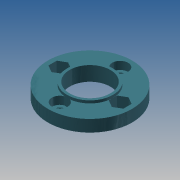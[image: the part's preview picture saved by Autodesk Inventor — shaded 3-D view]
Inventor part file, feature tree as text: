
AUTODESK INVENTOR PART (.ipt)
format: ipt  version: 2013 (Build 170138000, 138)  size: 146,944 bytes
history: native  units: mm
features: extrude x6, sketch x6, pattern_circular x2
ambient origin geometry x8: Origin, YZ Plane, XZ Plane, XY Plane, X Axis, Y Axis, Z Axis, Center Point
bodies: Solid1 (feature_tree)
feature tree (14):
  extrude  "Extrusion1"  Depth=4.5mm TaperAngle=0.0deg
  extrude  "Extrusion2"  Depth=1.0mm TaperAngle=0.0deg
  extrude  "Extrusion3"  Depth=1.0mm TaperAngle=0.0deg
  extrude  "Extrusion4"  Depth=3.5mm
  pattern_circular  "Circular Pattern1"  Count=4 Angle=360.0deg
  extrude  "Extrusion5"  Depth=3.0mm TaperAngle=0.0deg
  extrude  "Extrusion6"  Depth=5.5mm
  pattern_circular  "Circular Pattern2"  [2 undecoded]
  sketch  "Sketch1"  dims[d0=32.0mm d3=4.5mm d4=0.0mm]
  sketch  "Sketch2"  dims[d5=17.5mm d8=1.0mm d9=0.0mm]
  sketch  "Sketch3"  dims[d10=15.5mm d12=1.0mm d13=0.0mm]
  sketch  "Sketch4"  dims[d15=11.5mm d16=3.5mm]
  sketch  "Sketch5"  dims[d17=1.0mm d18=0.0mm d19=40.0mm d20=360.0deg]
  sketch  "Sketch6"  dims[d22=6.0mm d26=3.0mm d27=0.0mm d28=5.5mm d29=4.0mm d30=0.0mm d31=20.0mm d32=360.0deg]
note: 2 required parameter values undecoded (feature->parameter linkage not recoverable at this tier; creation-order binding heuristic only, values carry confidence <= 0.55)
